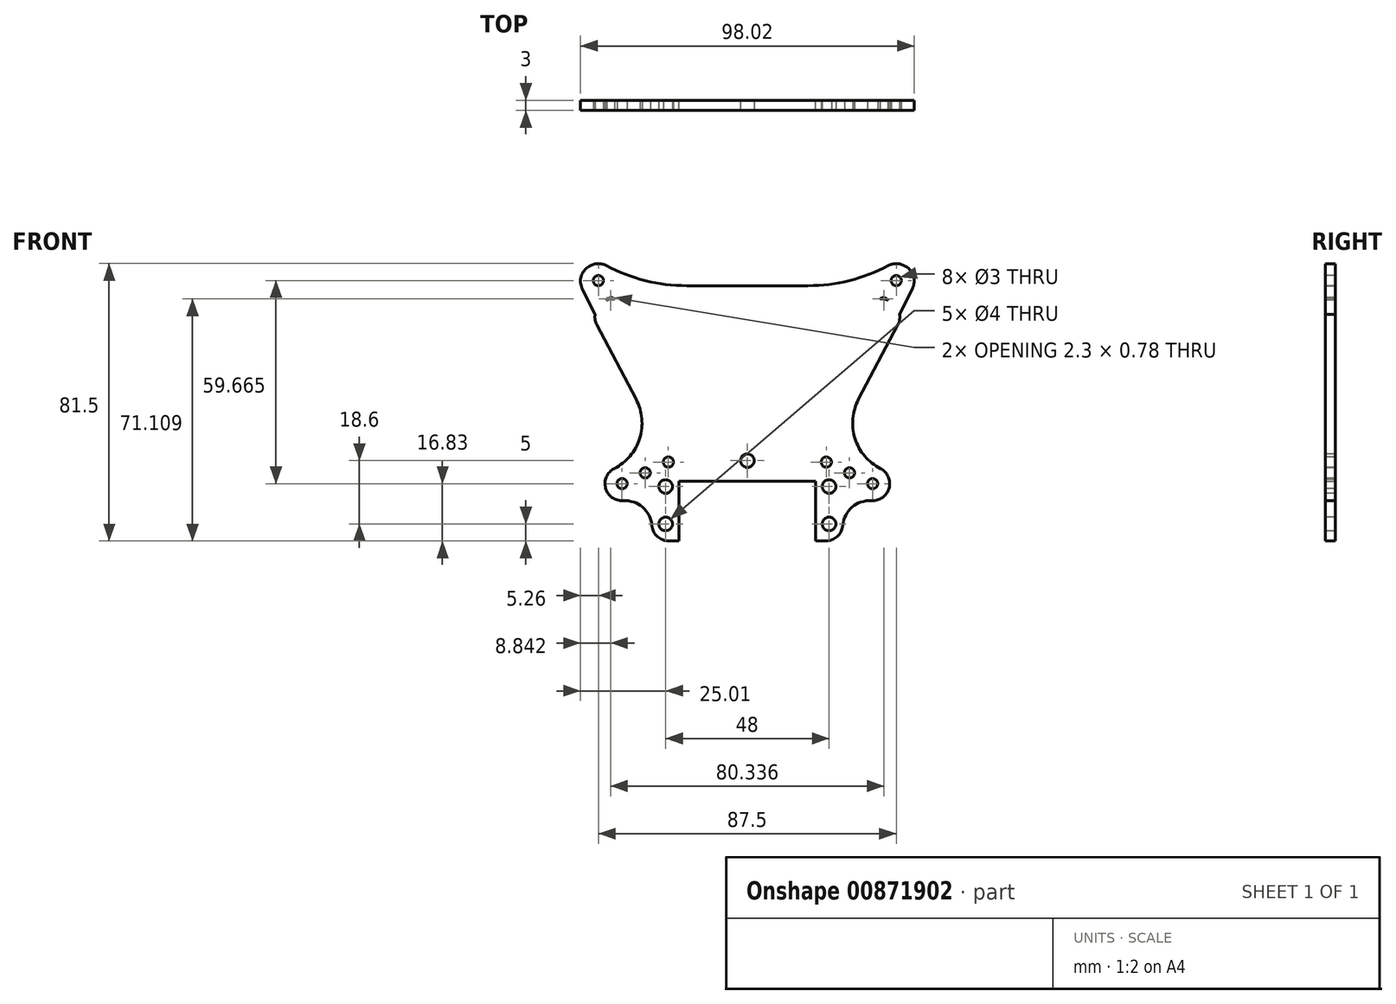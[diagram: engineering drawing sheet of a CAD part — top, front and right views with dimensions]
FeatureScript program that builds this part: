
annotation { "Feature Type Name" : "Feature", "Feature Type Description" : "" }
export const myFeature = defineFeature(function(context is Context, id is Id, definition is map)
    precondition{}
    {
        {
            var Q0;
            Q0=qCreatedBy(makeId("Front.planeOp"),FACE);
            var sketch = newSketch(context, id + "F0", { "sketchPlane" : qUnion([Q0])});
            skLineSegment(sketch, "E0.bottom", {"start": v(20.05, 57.6) * mm, "end": v(-20.05, 57.6) * mm, "construction": true});
            skLineSegment(sketch, "E0.top", {"start": v(20.05, 0) * mm, "end": v(-20.05, 0) * mm, "construction": true});
            skLineSegment(sketch, "E0.left", {"start": v(20.05, 57.6) * mm, "end": v(20.05, 0) * mm, "construction": true});
            skLineSegment(sketch, "E0.right", {"start": v(-20.05, 57.6) * mm, "end": v(-20.05, 0) * mm, "construction": true});
            skPoint(sketch, "E0.middle", {"position": v(0, 0) * mm});
            skLineSegment(sketch, "E1", {"start": v(20.05, 40) * mm, "end": v(28.05, 40) * mm});
            skLineSegment(sketch, "E2", {"start": v(0, 0) * mm, "end": v(0, 89.16) * mm, "construction": true});
            skLineSegment(sketch, "E3", {"start": v(0, 60) * mm, "end": v(30, 60) * mm, "construction": true});
            skLineSegment(sketch, "E4", {"start": v(0, 100) * mm, "end": v(35, 100) * mm, "construction": true});
            skLineSegment(sketch, "E5", {"start": v(39.3, 106.14) * mm, "end": v(30.7, 93.86) * mm, "construction": true});
            skLineSegment(sketch, "E6", {"start": v(23.2, 63.17) * mm, "end": v(36.8, 56.83) * mm, "construction": true});
            skPoint(sketch, "E7", {"position": v(23.2, 63.17) * mm});
            skPoint(sketch, "E8", {"position": v(30, 60) * mm});
            skPoint(sketch, "E9", {"position": v(36.8, 56.83) * mm});
            skPoint(sketch, "E10", {"position": v(30.7, 93.86) * mm});
            skPoint(sketch, "E11", {"position": v(39.3, 106.14) * mm});
            skLineSegment(sketch, "E12", {"start": v(25.32, 67.7) * mm, "end": v(43.44, 59.25) * mm});
            skLineSegment(sketch, "E13", {"start": v(28.05, 55.4) * mm, "end": v(39.22, 50.19) * mm});
            skLineSegment(sketch, "E14", {"start": v(39.22, 50.19) * mm, "end": v(43.44, 59.25) * mm});
            skLineSegment(sketch, "E15", {"start": v(46.27, 107.37) * mm, "end": v(38.07, 113.1) * mm});
            skLineSegment(sketch, "E16", {"start": v(38.07, 113.1) * mm, "end": v(32.4, 105) * mm});
            skLineSegment(sketch, "E17", {"start": v(32.4, 105) * mm, "end": v(0, 105) * mm});
            skLineSegment(sketch, "E18", {"start": v(28.05, 55.4) * mm, "end": v(28.05, 40) * mm});
            skLineSegment(sketch, "E19", {"start": v(20.05, 40) * mm, "end": v(20.05, 57.6) * mm, "construction": true});
            skLineSegment(sketch, "E20", {"start": v(20.05, 57.6) * mm, "end": v(0, 57.6) * mm});
            skLineSegment(sketch, "E21", {"start": v(20.05, 57.6) * mm, "end": v(20.05, 40) * mm});
            skPoint(sketch, "E22", {"position": v(24, 45) * mm});
            skPoint(sketch, "E23", {"position": v(24, 56) * mm});
            skPoint(sketch, "E24", {"position": v(0, 63.6) * mm});
            skLineSegment(sketch, "E25", {"start": v(0, 105) * mm, "end": v(0, 57.6) * mm});
            skLineSegment(sketch, "E26", {"start": v(46.27, 107.37) * mm, "end": v(25.32, 67.7) * mm});
            skSolve(sketch);
        }
        {
            var Q0;
            Q0=qCreatedBy(makeId("Front.planeOp"),FACE);
            var sketch = newSketch(context, id + "F1", { "sketchPlane" : qUnion([Q0])});
            skLineSegment(sketch, "E27.bottom", {"start": v(20.05, 57.6) * mm, "end": v(-20.05, 57.6) * mm, "construction": true});
            skLineSegment(sketch, "E27.top", {"start": v(20.05, 0) * mm, "end": v(-20.05, 0) * mm, "construction": true});
            skLineSegment(sketch, "E27.left", {"start": v(20.05, 57.6) * mm, "end": v(20.05, 0) * mm, "construction": true});
            skLineSegment(sketch, "E27.right", {"start": v(-20.05, 57.6) * mm, "end": v(-20.05, 0) * mm, "construction": true});
            skPoint(sketch, "E27.middle", {"position": v(0, 0) * mm});
            skLineSegment(sketch, "E28", {"start": v(20.05, 40) * mm, "end": v(28.05, 40) * mm});
            skLineSegment(sketch, "E29", {"start": v(0, 0) * mm, "end": v(0, 38.16) * mm, "construction": true});
            skLineSegment(sketch, "E30", {"start": v(0, 60) * mm, "end": v(30, 60) * mm, "construction": true});
            skLineSegment(sketch, "E31", {"start": v(0, 110) * mm, "end": v(40, 110) * mm, "construction": true});
            skLineSegment(sketch, "E32", {"start": v(43.75, 116.5) * mm, "end": v(36.25, 103.5) * mm, "construction": true});
            skLineSegment(sketch, "E33", {"start": v(23.2, 63.17) * mm, "end": v(36.8, 56.83) * mm, "construction": true});
            skPoint(sketch, "E34", {"position": v(23.2, 63.17) * mm});
            skPoint(sketch, "E35", {"position": v(30, 60) * mm});
            skPoint(sketch, "E36", {"position": v(36.8, 56.83) * mm});
            skPoint(sketch, "E37", {"position": v(36.25, 103.5) * mm});
            skPoint(sketch, "E38", {"position": v(43.75, 116.5) * mm});
            skLineSegment(sketch, "E39", {"start": v(50.58, 118.33) * mm, "end": v(25.32, 67.7) * mm});
            skLineSegment(sketch, "E40", {"start": v(25.32, 67.7) * mm, "end": v(43.44, 59.25) * mm});
            skLineSegment(sketch, "E41", {"start": v(28.05, 55.4) * mm, "end": v(39.22, 50.19) * mm});
            skLineSegment(sketch, "E42", {"start": v(39.22, 50.19) * mm, "end": v(43.44, 59.25) * mm});
            skLineSegment(sketch, "E43", {"start": v(50.58, 118.33) * mm, "end": v(41.92, 123.33) * mm});
            skLineSegment(sketch, "E44", {"start": v(41.92, 123.33) * mm, "end": v(37.11, 115) * mm});
            skLineSegment(sketch, "E45", {"start": v(37.11, 115) * mm, "end": v(0, 115) * mm});
            skLineSegment(sketch, "E46", {"start": v(28.05, 55.4) * mm, "end": v(28.05, 40) * mm});
            skLineSegment(sketch, "E47", {"start": v(20.05, 40) * mm, "end": v(20.05, 57.6) * mm, "construction": true});
            skLineSegment(sketch, "E48", {"start": v(20.05, 57.6) * mm, "end": v(0, 57.6) * mm});
            skLineSegment(sketch, "E49", {"start": v(20.05, 57.6) * mm, "end": v(20.05, 40) * mm});
            skPoint(sketch, "E50", {"position": v(24, 45) * mm});
            skPoint(sketch, "E51", {"position": v(24, 56) * mm});
            skPoint(sketch, "E52", {"position": v(0, 63.6) * mm});
            skLineSegment(sketch, "E53", {"start": v(0, 115) * mm, "end": v(0, 57.6) * mm});
            skSolve(sketch);
        }
        {
            assignVariable(context, id + "F2", {"name" : "thk", "anyValue" : 3});
        }
        {
            var Q0;
            Q0=qSketchRegion(id+"F0",true);
            extrude(context, id + "F3", {"entities" : qUnion([Q0]), "depth" : (getVariable(context, 'thk')) * mm, "offsetDistance" : 25 * mm});
        }
        {
            var Q0;
            Q0=sQuery(id+"F0.wireOp",VERTEX,"E9");
            var Q1;
            Q1=sQuery(id+"F0.wireOp",VERTEX,"E8");
            var Q2;
            Q2=sQuery(id+"F0.wireOp",VERTEX,"E7");
            var Q3;
            Q3=sQuery(id+"F0.wireOp",VERTEX,"E10");
            var Q4;
            Q4=sQuery(id+"F0.wireOp",VERTEX,"E11");
            var Q5;
            Q5=sQuery(id+"F0.wireOp",VERTEX,"E4.end");
            var Q6;
            Q6=makeQuery(id+"F3.opExtrude","SWEPT_BODY",BODY,{"disambiguationData":[OSD([sQuery(id+"F0.wireOp",EDGE,"E1"),sQuery(id+"F0.wireOp",EDGE,"OZeAhRmT-xPzG-nCHf-Kfua-VUdN2utOS6w8"),sQuery(id+"F0.wireOp",EDGE,"E12"),sQuery(id+"F0.wireOp",EDGE,"E13"),sQuery(id+"F0.wireOp",EDGE,"E14"),sQuery(id+"F0.wireOp",EDGE,"E15"),sQuery(id+"F0.wireOp",EDGE,"E16"),sQuery(id+"F0.wireOp",EDGE,"E17"),sQuery(id+"F0.wireOp",EDGE,"E18"),sQuery(id+"F0.wireOp",EDGE,"EVOupedH-QcjK-ySQv-SbbH-BYLRutnbYplv"),sQuery(id+"F0.wireOp",EDGE,"E20"),sQuery(id+"F0.wireOp",EDGE,"E21")])]});
            hole(context, id + "F4", {"style" : HoleStyle.SIMPLE, "endStyle" : HoleEndStyle.THROUGH, "oppositeDirection" : true, "holeDiameter" : 3 * mm, "majorDiameter" : 5 * mm, "isTappedThrough" : true, "tappedDepth" : 12 * mm, "tapClearance" : 3, "locations" : qUnion([Q0, Q1, Q2, Q3, Q4, Q5]), "scope" : qUnion([Q6])});
        }
        {
            var Q0;
            Q0=sQuery(id+"F0.wireOp",VERTEX,"E23");
            var Q1;
            Q1=sQuery(id+"F0.wireOp",VERTEX,"E22");
            var Q2;
            Q2=sQuery(id+"F0.wireOp",VERTEX,"E24");
            var Q3;
            Q3=makeQuery(id+"F3.opExtrude","SWEPT_BODY",BODY,{"disambiguationData":[OSD([sQuery(id+"F0.wireOp",EDGE,"E1"),sQuery(id+"F0.wireOp",EDGE,"OZeAhRmT-xPzG-nCHf-Kfua-VUdN2utOS6w8"),sQuery(id+"F0.wireOp",EDGE,"E12"),sQuery(id+"F0.wireOp",EDGE,"E13"),sQuery(id+"F0.wireOp",EDGE,"E14"),sQuery(id+"F0.wireOp",EDGE,"E15"),sQuery(id+"F0.wireOp",EDGE,"E16"),sQuery(id+"F0.wireOp",EDGE,"E17"),sQuery(id+"F0.wireOp",EDGE,"E18"),sQuery(id+"F0.wireOp",EDGE,"EVOupedH-QcjK-ySQv-SbbH-BYLRutnbYplv"),sQuery(id+"F0.wireOp",EDGE,"E20"),sQuery(id+"F0.wireOp",EDGE,"E21")])]});
            hole(context, id + "F5", {"style" : HoleStyle.SIMPLE, "endStyle" : HoleEndStyle.THROUGH, "oppositeDirection" : true, "holeDiameter" : 4 * mm, "majorDiameter" : 5 * mm, "isTappedThrough" : true, "tappedDepth" : 12 * mm, "tapClearance" : 3, "locations" : qUnion([Q0, Q1, Q2]), "scope" : qUnion([Q3])});
        }
        {
            var Q0;
            Q0=makeQuery(id+"F3.opExtrude","SWEPT_EDGE",EDGE,{"disambiguationData":[OSD([sQuery(id+"F0.wireOp",EDGE,"E15"),sQuery(id+"F0.wireOp",EDGE,"E16")])]});
            var Q1;
            Q1=makeQuery(id+"F3.opExtrude","SWEPT_EDGE",EDGE,{"disambiguationData":[OSD([sQuery(id+"F0.wireOp",EDGE,"OZeAhRmT-xPzG-nCHf-Kfua-VUdN2utOS6w8"),sQuery(id+"F0.wireOp",EDGE,"E15")])]});
            var Q2;
            Q2=makeQuery(id+"F3.opExtrude","SWEPT_EDGE",EDGE,{"disambiguationData":[OSD([sQuery(id+"F0.wireOp",EDGE,"E12"),sQuery(id+"F0.wireOp",EDGE,"E14")])]});
            var Q3;
            Q3=makeQuery(id+"F3.opExtrude","SWEPT_EDGE",EDGE,{"disambiguationData":[OSD([sQuery(id+"F0.wireOp",EDGE,"E13"),sQuery(id+"F0.wireOp",EDGE,"E14")])]});
            var Q4;
            Q4=makeQuery(id+"F3.opExtrude","SWEPT_EDGE",EDGE,{"disambiguationData":[OSD([sQuery(id+"F0.wireOp",EDGE,"E1"),sQuery(id+"F0.wireOp",EDGE,"E18")])]});
            fillet(context, id + "F6", {"entities" : qUnion([Q0, Q1, Q2, Q3, Q4]), "radius" : 5 * mm, "tangentPropagation" : true, "allowEdgeOverflow" : false});
        }
        {
            var Q0;
            Q0=makeQuery(id+"F3.opExtrude","SWEPT_EDGE",EDGE,{"disambiguationData":[OSD([sQuery(id+"F0.wireOp",EDGE,"E16"),sQuery(id+"F0.wireOp",EDGE,"E17")])]});
            fillet(context, id + "F7", {"entities" : qUnion([Q0]), "radius" : 45 * mm, "tangentPropagation" : true, "allowEdgeOverflow" : false});
        }
        {
            var Q0;
            Q0=makeQuery(id+"F3.opExtrude","SWEPT_EDGE",EDGE,{"disambiguationData":[OSD([sQuery(id+"F0.wireOp",EDGE,"OZeAhRmT-xPzG-nCHf-Kfua-VUdN2utOS6w8"),sQuery(id+"F0.wireOp",EDGE,"E12")])]});
            fillet(context, id + "F8", {"entities" : qUnion([Q0]), "radius" : 15 * mm, "tangentPropagation" : true, "allowEdgeOverflow" : false});
        }
        {
            var Q0;
            Q0=makeQuery(id+"F3.opExtrude","SWEPT_EDGE",EDGE,{"disambiguationData":[OSD([sQuery(id+"F0.wireOp",EDGE,"E13"),sQuery(id+"F0.wireOp",EDGE,"E18")])]});
            fillet(context, id + "F9", {"entities" : qUnion([Q0]), "radius" : 8 * mm, "tangentPropagation" : true, "allowEdgeOverflow" : false});
        }
        {
            var Q0;
            Q0=makeQuery(id+"F3.opExtrude","SWEPT_BODY",BODY,{"disambiguationData":[OSD([sQuery(id+"F0.wireOp",EDGE,"E1"),sQuery(id+"F0.wireOp",EDGE,"OZeAhRmT-xPzG-nCHf-Kfua-VUdN2utOS6w8"),sQuery(id+"F0.wireOp",EDGE,"E12"),sQuery(id+"F0.wireOp",EDGE,"E13"),sQuery(id+"F0.wireOp",EDGE,"E14"),sQuery(id+"F0.wireOp",EDGE,"E15"),sQuery(id+"F0.wireOp",EDGE,"E16"),sQuery(id+"F0.wireOp",EDGE,"E17"),sQuery(id+"F0.wireOp",EDGE,"E18"),sQuery(id+"F0.wireOp",EDGE,"EVOupedH-QcjK-ySQv-SbbH-BYLRutnbYplv"),sQuery(id+"F0.wireOp",EDGE,"E20"),sQuery(id+"F0.wireOp",EDGE,"E21")])]});
            var Q1;
            Q1=qCreatedBy(makeId("Right.planeOp"),FACE);
            mirror(context, id + "F10", {"operationType" : NewBodyOperationType.ADD, "entities" : qUnion([Q0]), "mirrorPlane" : qUnion([Q1])});
        }
        {
            var Q0;
            Q0=qSketchRegion(id+"F1",true);
            extrude(context, id + "F11", {"entities" : qUnion([Q0]), "depth" : (getVariable(context, 'thk')) * mm, "offsetDistance" : 25 * mm});
        }
        {
            var Q0;
            Q0=sQuery(id+"F1.wireOp",VERTEX,"E37");
            var Q1;
            Q1=sQuery(id+"F1.wireOp",VERTEX,"E31.end");
            var Q2;
            Q2=sQuery(id+"F1.wireOp",VERTEX,"E38");
            var Q3;
            Q3=sQuery(id+"F1.wireOp",VERTEX,"E30.end");
            var Q4;
            Q4=sQuery(id+"F1.wireOp",VERTEX,"E36");
            var Q5;
            Q5=sQuery(id+"F1.wireOp",VERTEX,"E33.start");
            var Q6;
            Q6=makeQuery(id+"F11.opExtrude","SWEPT_BODY",BODY,{"disambiguationData":[OSD([sQuery(id+"F1.wireOp",EDGE,"E28"),sQuery(id+"F1.wireOp",EDGE,"E39"),sQuery(id+"F1.wireOp",EDGE,"E40"),sQuery(id+"F1.wireOp",EDGE,"E41"),sQuery(id+"F1.wireOp",EDGE,"E42"),sQuery(id+"F1.wireOp",EDGE,"E43"),sQuery(id+"F1.wireOp",EDGE,"E44"),sQuery(id+"F1.wireOp",EDGE,"E45"),sQuery(id+"F1.wireOp",EDGE,"E46"),sQuery(id+"F1.wireOp",EDGE,"E48"),sQuery(id+"F1.wireOp",EDGE,"E49"),sQuery(id+"F1.wireOp",EDGE,"E53")])]});
            hole(context, id + "F12", {"style" : HoleStyle.SIMPLE, "endStyle" : HoleEndStyle.THROUGH, "oppositeDirection" : true, "holeDiameter" : 3 * mm, "majorDiameter" : 5 * mm, "isTappedThrough" : true, "tappedDepth" : 12 * mm, "tapClearance" : 3, "locations" : qUnion([Q0, Q1, Q2, Q3, Q4, Q5]), "scope" : qUnion([Q6])});
        }
        {
            var Q0;
            Q0=sQuery(id+"F1.wireOp",VERTEX,"E52");
            var Q1;
            Q1=sQuery(id+"F1.wireOp",VERTEX,"E51");
            var Q2;
            Q2=sQuery(id+"F1.wireOp",VERTEX,"E50");
            var Q3;
            Q3=makeQuery(id+"F11.opExtrude","SWEPT_BODY",BODY,{"disambiguationData":[OSD([sQuery(id+"F1.wireOp",EDGE,"E28"),sQuery(id+"F1.wireOp",EDGE,"E39"),sQuery(id+"F1.wireOp",EDGE,"E40"),sQuery(id+"F1.wireOp",EDGE,"E41"),sQuery(id+"F1.wireOp",EDGE,"E42"),sQuery(id+"F1.wireOp",EDGE,"E43"),sQuery(id+"F1.wireOp",EDGE,"E44"),sQuery(id+"F1.wireOp",EDGE,"E45"),sQuery(id+"F1.wireOp",EDGE,"E46"),sQuery(id+"F1.wireOp",EDGE,"E48"),sQuery(id+"F1.wireOp",EDGE,"E49"),sQuery(id+"F1.wireOp",EDGE,"E53")])]});
            hole(context, id + "F13", {"style" : HoleStyle.SIMPLE, "endStyle" : HoleEndStyle.THROUGH, "oppositeDirection" : true, "holeDiameter" : 4 * mm, "majorDiameter" : 5 * mm, "isTappedThrough" : true, "tappedDepth" : 12 * mm, "tapClearance" : 3, "locations" : qUnion([Q0, Q1, Q2]), "scope" : qUnion([Q3])});
        }
        {
            var Q0;
            Q0=makeQuery(id+"F11.opExtrude","SWEPT_EDGE",EDGE,{"disambiguationData":[OSD([sQuery(id+"F1.wireOp",EDGE,"E39"),sQuery(id+"F1.wireOp",EDGE,"E43")])]});
            var Q1;
            Q1=makeQuery(id+"F11.opExtrude","SWEPT_EDGE",EDGE,{"disambiguationData":[OSD([sQuery(id+"F1.wireOp",EDGE,"E43"),sQuery(id+"F1.wireOp",EDGE,"E44")])]});
            var Q2;
            Q2=makeQuery(id+"F11.opExtrude","SWEPT_EDGE",EDGE,{"disambiguationData":[OSD([sQuery(id+"F1.wireOp",EDGE,"E40"),sQuery(id+"F1.wireOp",EDGE,"E42")])]});
            var Q3;
            Q3=makeQuery(id+"F11.opExtrude","SWEPT_EDGE",EDGE,{"disambiguationData":[OSD([sQuery(id+"F1.wireOp",EDGE,"E41"),sQuery(id+"F1.wireOp",EDGE,"E42")])]});
            var Q4;
            Q4=makeQuery(id+"F11.opExtrude","SWEPT_EDGE",EDGE,{"disambiguationData":[OSD([sQuery(id+"F1.wireOp",EDGE,"E28"),sQuery(id+"F1.wireOp",EDGE,"E46")])]});
            fillet(context, id + "F14", {"entities" : qUnion([Q0, Q1, Q2, Q3, Q4]), "radius" : 5 * mm, "tangentPropagation" : true, "allowEdgeOverflow" : false});
        }
        {
            var Q0;
            Q0=makeQuery(id+"F11.opExtrude","SWEPT_EDGE",EDGE,{"disambiguationData":[OSD([sQuery(id+"F1.wireOp",EDGE,"E44"),sQuery(id+"F1.wireOp",EDGE,"E45")])]});
            fillet(context, id + "F15", {"entities" : qUnion([Q0]), "radius" : 50 * mm, "tangentPropagation" : true, "allowEdgeOverflow" : false});
        }
        {
            var Q0;
            Q0=makeQuery(id+"F11.opExtrude","SWEPT_EDGE",EDGE,{"disambiguationData":[OSD([sQuery(id+"F1.wireOp",EDGE,"E39"),sQuery(id+"F1.wireOp",EDGE,"E40")])]});
            fillet(context, id + "F16", {"entities" : qUnion([Q0]), "radius" : 15 * mm, "tangentPropagation" : true, "allowEdgeOverflow" : false});
        }
        {
            var Q0;
            Q0=makeQuery(id+"F11.opExtrude","SWEPT_EDGE",EDGE,{"disambiguationData":[OSD([sQuery(id+"F1.wireOp",EDGE,"E41"),sQuery(id+"F1.wireOp",EDGE,"E46")])]});
            fillet(context, id + "F17", {"entities" : qUnion([Q0]), "radius" : 8 * mm, "tangentPropagation" : true, "allowEdgeOverflow" : false});
        }
        {
            var Q0;
            Q0=makeQuery(id+"F11.opExtrude","SWEPT_BODY",BODY,{"disambiguationData":[OSD([sQuery(id+"F1.wireOp",EDGE,"E28"),sQuery(id+"F1.wireOp",EDGE,"E39"),sQuery(id+"F1.wireOp",EDGE,"E40"),sQuery(id+"F1.wireOp",EDGE,"E41"),sQuery(id+"F1.wireOp",EDGE,"E42"),sQuery(id+"F1.wireOp",EDGE,"E43"),sQuery(id+"F1.wireOp",EDGE,"E44"),sQuery(id+"F1.wireOp",EDGE,"E45"),sQuery(id+"F1.wireOp",EDGE,"E46"),sQuery(id+"F1.wireOp",EDGE,"E48"),sQuery(id+"F1.wireOp",EDGE,"E49"),sQuery(id+"F1.wireOp",EDGE,"E53")])]});
            var Q1;
            Q1=qCreatedBy(makeId("Right.planeOp"),FACE);
            mirror(context, id + "F18", {"operationType" : NewBodyOperationType.ADD, "entities" : qUnion([Q0]), "mirrorPlane" : qUnion([Q1])});
        }
    });
